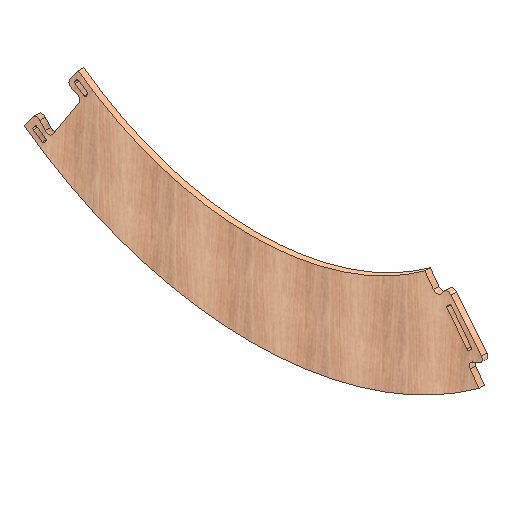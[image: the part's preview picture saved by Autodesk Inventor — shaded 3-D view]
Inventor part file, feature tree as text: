
AUTODESK INVENTOR PART (.ipt)
format: ipt  version: 2021 (Build 250183000, 183)  size: 289,280 bytes
history: native  units: mm
features: other x2, extrude x2, hole x1
ambient origin geometry x8: Origin, YZ Plane, XZ Plane, XY Plane, X Axis, Y Axis, Z Axis, Center Point
bodies: Solid1 (feature_tree)
feature tree (5):
  other  "CONTOURS"
  hole  "HOLES"  [1 undecoded]
  other  "LETTERS"
  extrude  "Extrusion1"  Depth=18.0mm TaperAngle=0.0deg
  extrude  "Extrusion2"  [1 undecoded]
note: 2 required parameter values undecoded (feature->parameter linkage not recoverable at this tier; creation-order binding heuristic only, values carry confidence <= 0.55)
